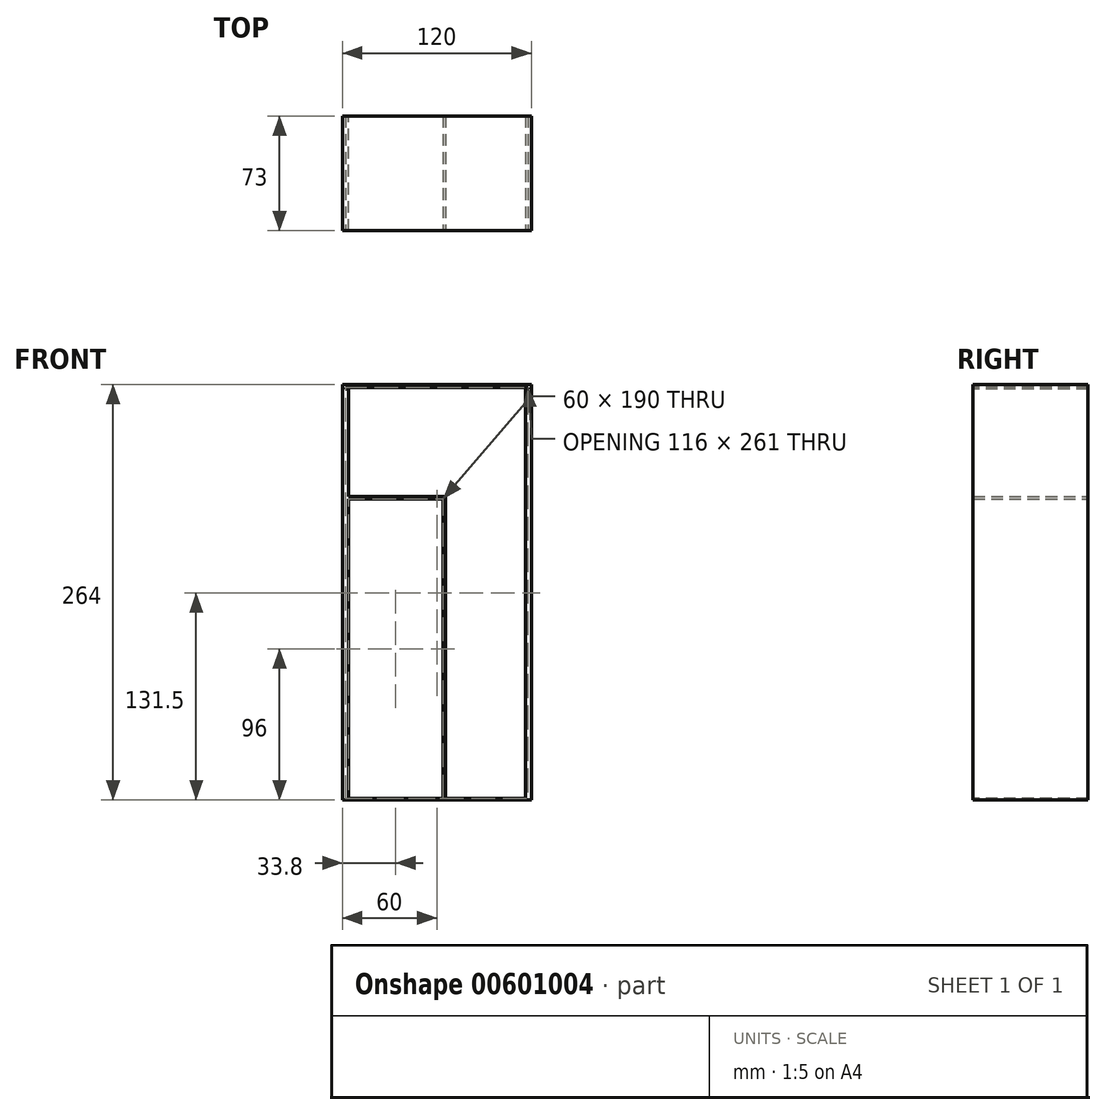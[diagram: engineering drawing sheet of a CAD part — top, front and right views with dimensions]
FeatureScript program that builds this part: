
annotation { "Feature Type Name" : "Feature", "Feature Type Description" : "" }
export const myFeature = defineFeature(function(context is Context, id is Id, definition is map)
    precondition{}
    {
        {
            var Q0;
            Q0=qCreatedBy(makeId("Top.planeOp"),FACE);
            var sketch = newSketch(context, id + "F0", { "sketchPlane" : qUnion([Q0])});
            skLineSegment(sketch, "E0", {"start": v(-100, 0) * mm, "end": v(-100, 73) * mm});
            skLineSegment(sketch, "E1", {"start": v(-100, 73) * mm, "end": v(20, 73) * mm});
            skLineSegment(sketch, "E2", {"start": v(20, 73) * mm, "end": v(20, 0) * mm});
            skLineSegment(sketch, "E3", {"start": v(20, 0) * mm, "end": v(-100, 0) * mm});
            skSolve(sketch);
        }
        {
            var Q0;
            Q0=makeQuery(id+"F0.imprint","IMPRINT",FACE,{"disambiguationData":[TD([[makeQuery(id+"F0.imprint","IMPRINT",EDGE,{"derivedFrom":sQuery(id+"F0.wireOp",EDGE,"E0")}),-1.0]])]});
            extrude(context, id + "F1", {"entities" : qUnion([Q0]), "depth" : 1 * mm, "offsetDistance" : 25 * mm});
        }
        {
            var Q0;
            Q0=makeQuery(id+"F1.opExtrude","CAP_FACE",FACE,{"disambiguationData":[OSD([sQuery(id+"F0.wireOp",EDGE,"E0"),sQuery(id+"F0.wireOp",EDGE,"E1"),sQuery(id+"F0.wireOp",EDGE,"E2"),sQuery(id+"F0.wireOp",EDGE,"E3")])],"isStart":false});
            var sketch = newSketch(context, id + "F2", { "sketchPlane" : qUnion([Q0])});
            skLineSegment(sketch, "E4.bottom", {"start": v(-100, 73) * mm, "end": v(-98, 73) * mm});
            skLineSegment(sketch, "E4.top", {"start": v(-100, 0) * mm, "end": v(-98, 0) * mm});
            skLineSegment(sketch, "E4.left", {"start": v(-100, 73) * mm, "end": v(-100, 0) * mm});
            skLineSegment(sketch, "E4.right", {"start": v(-98, 73) * mm, "end": v(-98, 0) * mm});
            skLineSegment(sketch, "E5.bottom", {"start": v(20, 73) * mm, "end": v(18, 73) * mm});
            skLineSegment(sketch, "E5.top", {"start": v(20, 0) * mm, "end": v(18, 0) * mm});
            skLineSegment(sketch, "E5.left", {"start": v(20, 73) * mm, "end": v(20, 0) * mm});
            skLineSegment(sketch, "E5.right", {"start": v(18, 73) * mm, "end": v(18, 0) * mm});
            skSolve(sketch);
        }
        {
            var Q0;
            Q0=makeQuery(id+"F2.imprint","IMPRINT",FACE,{"disambiguationData":[TD([[makeQuery(id+"F2.imprint","IMPRINT",EDGE,{"derivedFrom":sQuery(id+"F2.wireOp",EDGE,"E4.bottom")}),-1.0]])]});
            var Q1;
            Q1=makeQuery(id+"F2.imprint","IMPRINT",FACE,{"disambiguationData":[TD([[makeQuery(id+"F2.imprint","IMPRINT",EDGE,{"derivedFrom":sQuery(id+"F2.wireOp",EDGE,"E5.bottom")}),-1.0]])]});
            extrude(context, id + "F3", {"entities" : qUnion([Q0, Q1]), "operationType" : NewBodyOperationType.ADD, "depth" : 261 * mm, "offsetDistance" : 25 * mm});
        }
        {
            var Q0;
            Q0=makeQuery(id+"F3.opExtrude","CAP_FACE",FACE,{"disambiguationData":[OSD([sQuery(id+"F2.wireOp",EDGE,"E5.bottom"),sQuery(id+"F2.wireOp",EDGE,"E5.top"),sQuery(id+"F2.wireOp",EDGE,"E5.left"),sQuery(id+"F2.wireOp",EDGE,"E5.right")])],"isStart":false});
            var sketch = newSketch(context, id + "F4", { "sketchPlane" : qUnion([Q0])});
            skLineSegment(sketch, "E6.bottom", {"start": v(20, 0) * mm, "end": v(-100, 0) * mm});
            skLineSegment(sketch, "E6.top", {"start": v(20, 73) * mm, "end": v(-100, 73) * mm});
            skLineSegment(sketch, "E6.left", {"start": v(20, 0) * mm, "end": v(20, 73) * mm});
            skLineSegment(sketch, "E6.right", {"start": v(-100, 0) * mm, "end": v(-100, 73) * mm});
            skSolve(sketch);
        }
        {
            var Q0;
            Q0 = qSketchRegion(id + "F4", true);
            extrude(context, id + "F5", {"entities" : qUnion([Q0]), "operationType" : NewBodyOperationType.ADD, "depth" : 2 * mm, "offsetDistance" : 25 * mm});
        }
        {
            var Q0;
            Q0=makeQuery(id+"F1.opExtrude","CAP_FACE",FACE,{"disambiguationData":[OSD([sQuery(id+"F0.wireOp",EDGE,"E0"),sQuery(id+"F0.wireOp",EDGE,"E1"),sQuery(id+"F0.wireOp",EDGE,"E2"),sQuery(id+"F0.wireOp",EDGE,"E3")])],"isStart":false});
            var sketch = newSketch(context, id + "F6", { "sketchPlane" : qUnion([Q0])});
            skLineSegment(sketch, "E7.bottom", {"start": v(-98, 73) * mm, "end": v(-96.2, 73) * mm});
            skLineSegment(sketch, "E7.top", {"start": v(-98, 0) * mm, "end": v(-96.2, 0) * mm});
            skLineSegment(sketch, "E7.left", {"start": v(-98, 73) * mm, "end": v(-98, 0) * mm});
            skLineSegment(sketch, "E7.right", {"start": v(-96.2, 73) * mm, "end": v(-96.2, 0) * mm});
            skLineSegment(sketch, "E8.bottom", {"start": v(18, 73) * mm, "end": v(16.2, 73) * mm});
            skLineSegment(sketch, "E8.top", {"start": v(18, 0) * mm, "end": v(16.2, 0) * mm});
            skLineSegment(sketch, "E8.left", {"start": v(18, 73) * mm, "end": v(18, 0) * mm});
            skLineSegment(sketch, "E8.right", {"start": v(16.2, 73) * mm, "end": v(16.2, 0) * mm});
            skSolve(sketch);
        }
        {
            var Q0;
            Q0 = qSketchRegion(id + "F6", true);
            extrude(context, id + "F7", {"entities" : qUnion([Q0]), "operationType" : NewBodyOperationType.ADD, "depth" : 260 * mm, "offsetDistance" : 25 * mm});
        }
        {
            var Q0;
            Q0=makeQuery(id+"F1.opExtrude","CAP_FACE",FACE,{"disambiguationData":[OSD([sQuery(id+"F0.wireOp",EDGE,"E0"),sQuery(id+"F0.wireOp",EDGE,"E1"),sQuery(id+"F0.wireOp",EDGE,"E2"),sQuery(id+"F0.wireOp",EDGE,"E3")])],"isStart":false});
            var sketch = newSketch(context, id + "F8", { "sketchPlane" : qUnion([Q0])});
            skLineSegment(sketch, "E9.bottom", {"start": v(-96.2, 0) * mm, "end": v(-36.2, 0) * mm});
            skLineSegment(sketch, "E9.top", {"start": v(-96.2, 73) * mm, "end": v(-36.2, 73) * mm});
            skLineSegment(sketch, "E9.left", {"start": v(-96.2, 0) * mm, "end": v(-96.2, 73) * mm});
            skLineSegment(sketch, "E9.right", {"start": v(-36.2, 0) * mm, "end": v(-36.2, 73) * mm});
            skSolve(sketch);
        }
        {
            var Q0;
            Q0=makeQuery(id+"F1.opExtrude","CAP_FACE",FACE,{"disambiguationData":[OSD([sQuery(id+"F0.wireOp",EDGE,"E0"),sQuery(id+"F0.wireOp",EDGE,"E1"),sQuery(id+"F0.wireOp",EDGE,"E2"),sQuery(id+"F0.wireOp",EDGE,"E3")])],"isStart":false});
            var sketch = newSketch(context, id + "F9", { "sketchPlane" : qUnion([Q0])});
            skLineSegment(sketch, "E10.bottom", {"start": v(-36.2, 73) * mm, "end": v(-34.4, 73) * mm});
            skLineSegment(sketch, "E10.top", {"start": v(-36.2, 0) * mm, "end": v(-34.4, 0) * mm});
            skLineSegment(sketch, "E10.left", {"start": v(-36.2, 73) * mm, "end": v(-36.2, 0) * mm});
            skLineSegment(sketch, "E10.right", {"start": v(-34.4, 73) * mm, "end": v(-34.4, 0) * mm});
            skSolve(sketch);
        }
        {
            var Q0;
            Q0 = qSketchRegion(id + "F9", true);
            extrude(context, id + "F10", {"entities" : qUnion([Q0]), "operationType" : NewBodyOperationType.ADD, "depth" : 190 * mm, "offsetDistance" : 25 * mm});
        }
        {
            var Q0;
            Q0=makeQuery(id+"F10.opExtrude","CAP_FACE",FACE,{"disambiguationData":[OSD([sQuery(id+"F9.wireOp",EDGE,"E10.bottom"),sQuery(id+"F9.wireOp",EDGE,"E10.top"),sQuery(id+"F9.wireOp",EDGE,"E10.left"),sQuery(id+"F9.wireOp",EDGE,"E10.right")])],"isStart":false});
            var sketch = newSketch(context, id + "F11", { "sketchPlane" : qUnion([Q0])});
            skLineSegment(sketch, "E11.bottom", {"start": v(-34.4, 0) * mm, "end": v(-96.2, 0) * mm});
            skLineSegment(sketch, "E11.top", {"start": v(-34.4, 73) * mm, "end": v(-96.2, 73) * mm});
            skLineSegment(sketch, "E11.left", {"start": v(-34.4, 0) * mm, "end": v(-34.4, 73) * mm});
            skLineSegment(sketch, "E11.right", {"start": v(-96.2, 0) * mm, "end": v(-96.2, 73) * mm});
            skSolve(sketch);
        }
        {
            var Q0;
            {var subQ2=sQuery(id+"F11.wireOp",EDGE,"E11.right");Q0=makeQuery(id+"F11.imprint","IMPRINT",FACE,{"disambiguationData":[TD([[makeQuery(id+"F11.imprint","IMPRINT",EDGE,{"derivedFrom":subQ2}),-1.0]])]});}
            var Q1;
            {var subQ2=sQuery(id+"F11.wireOp",EDGE,"E11.left");Q1=makeQuery(id+"F11.imprint","IMPRINT",FACE,{"disambiguationData":[TD([[makeQuery(id+"F11.imprint","IMPRINT",EDGE,{"derivedFrom":subQ2}),-1.0]])]});}
            extrude(context, id + "F12", {"entities" : qUnion([Q0, Q1]), "operationType" : NewBodyOperationType.ADD, "depth" : 1.8 * mm, "offsetDistance" : 25 * mm});
        }
    });
